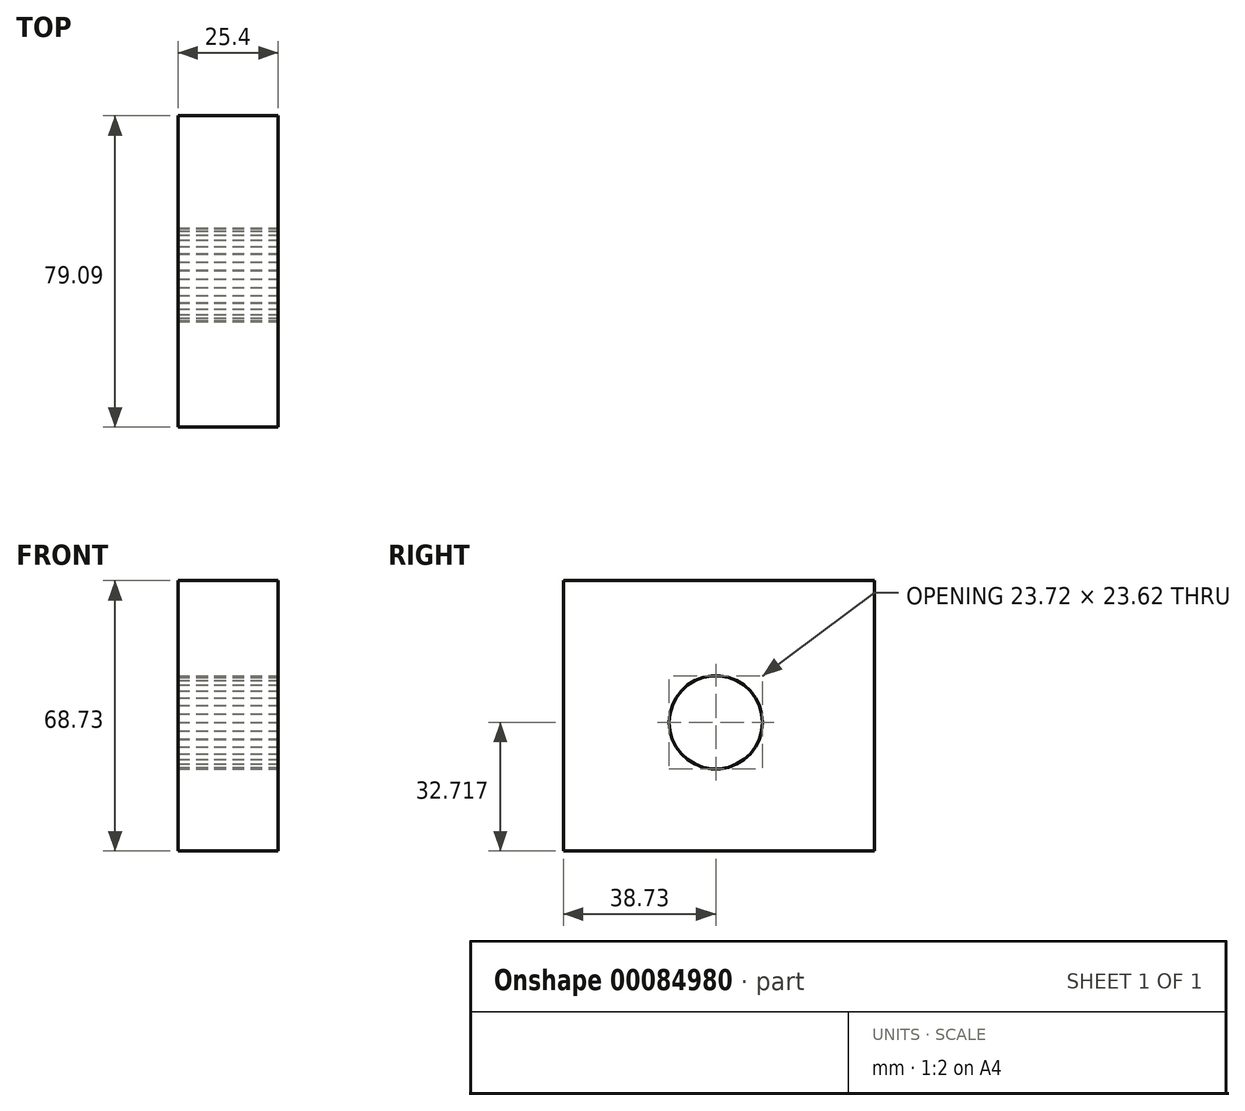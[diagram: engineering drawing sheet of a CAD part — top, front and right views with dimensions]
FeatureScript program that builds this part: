
annotation { "Feature Type Name" : "Feature", "Feature Type Description" : "" }
export const myFeature = defineFeature(function(context is Context, id is Id, definition is map)
    precondition{}
    {
        {
            var Q0;
            Q0=qCreatedBy(makeId("Right.planeOp"),FACE);
            var sketch = newSketch(context, id + "F0", { "sketchPlane" : qUnion([Q0])});
            skLineSegment(sketch, "E0.bottom", {"start": v(-38.73, 43.14) * mm, "end": v(40.36, 43.14) * mm});
            skLineSegment(sketch, "E0.top", {"start": v(-38.73, -25.6) * mm, "end": v(40.36, -25.6) * mm});
            skLineSegment(sketch, "E0.left", {"start": v(-38.73, 43.14) * mm, "end": v(-38.73, -25.6) * mm});
            skLineSegment(sketch, "E0.right", {"start": v(40.36, 43.14) * mm, "end": v(40.36, -25.6) * mm});
            skSolve(sketch);
        }
        {
            var Q0;
            Q0 = qSketchRegion(id + "F0", true);
            extrude(context, id + "F1", {"entities" : qUnion([Q0]), "depth" : 25.4 * mm, "offsetDistance" : 25.4 * mm});
        }
        {
            var Q0;
            Q0=makeQuery(id+"F1.opExtrude","CAP_FACE",FACE,{"disambiguationData":[OSD([sQuery(id+"F0.wireOp",EDGE,"E0.bottom"),sQuery(id+"F0.wireOp",EDGE,"E0.top"),sQuery(id+"F0.wireOp",EDGE,"E0.left"),sQuery(id+"F0.wireOp",EDGE,"E0.right")])],"isStart":false});
            var sketch = newSketch(context, id + "F2", { "sketchPlane" : qUnion([Q0])});
            skCircle(sketch, "E1.cCircle", {"center": v(0, 7.13) * mm, "radius": 11.8 * mm, "construction": true});
            skLineSegment(sketch, "E1.0", {"start": v(10.07, 0.87) * mm, "end": v(8.75, -0.87) * mm});
            skLineSegment(sketch, "E1.1", {"start": v(8.75, -0.87) * mm, "end": v(7.13, -2.34) * mm});
            skLineSegment(sketch, "E1.2", {"start": v(7.13, -2.34) * mm, "end": v(5.27, -3.5) * mm});
            skLineSegment(sketch, "E1.3", {"start": v(5.27, -3.5) * mm, "end": v(3.23, -4.28) * mm});
            skLineSegment(sketch, "E1.4", {"start": v(3.23, -4.28) * mm, "end": v(1.08, -4.68) * mm});
            skLineSegment(sketch, "E1.5", {"start": v(1.08, -4.68) * mm, "end": v(-1.1, -4.68) * mm});
            skLineSegment(sketch, "E1.6", {"start": v(-1.1, -4.68) * mm, "end": v(-3.26, -4.27) * mm});
            skLineSegment(sketch, "E1.7", {"start": v(-3.26, -4.27) * mm, "end": v(-5.3, -3.48) * mm});
            skLineSegment(sketch, "E1.8", {"start": v(-5.3, -3.48) * mm, "end": v(-7.16, -2.33) * mm});
            skLineSegment(sketch, "E1.9", {"start": v(-7.16, -2.33) * mm, "end": v(-8.77, -0.85) * mm});
            skLineSegment(sketch, "E1.10", {"start": v(-8.77, -0.85) * mm, "end": v(-10.09, 0.9) * mm});
            skLineSegment(sketch, "E1.11", {"start": v(-10.09, 0.9) * mm, "end": v(-11.06, 2.86) * mm});
            skLineSegment(sketch, "E1.12", {"start": v(-11.06, 2.86) * mm, "end": v(-11.66, 4.96) * mm});
            skLineSegment(sketch, "E1.13", {"start": v(-11.66, 4.96) * mm, "end": v(-11.86, 7.14) * mm});
            skLineSegment(sketch, "E1.14", {"start": v(-11.86, 7.14) * mm, "end": v(-11.65, 9.32) * mm});
            skLineSegment(sketch, "E1.15", {"start": v(-11.65, 9.32) * mm, "end": v(-11.05, 11.42) * mm});
            skLineSegment(sketch, "E1.16", {"start": v(-11.05, 11.42) * mm, "end": v(-10.07, 13.38) * mm});
            skLineSegment(sketch, "E1.17", {"start": v(-10.07, 13.38) * mm, "end": v(-8.75, 15.13) * mm});
            skLineSegment(sketch, "E1.18", {"start": v(-8.75, 15.13) * mm, "end": v(-7.13, 16.6) * mm});
            skLineSegment(sketch, "E1.19", {"start": v(-7.13, 16.6) * mm, "end": v(-5.27, 17.75) * mm});
            skLineSegment(sketch, "E1.20", {"start": v(-5.27, 17.75) * mm, "end": v(-3.23, 18.54) * mm});
            skLineSegment(sketch, "E1.21", {"start": v(-3.23, 18.54) * mm, "end": v(-1.08, 18.94) * mm});
            skLineSegment(sketch, "E1.22", {"start": v(-1.08, 18.94) * mm, "end": v(1.1, 18.93) * mm});
            skLineSegment(sketch, "E1.23", {"start": v(1.1, 18.93) * mm, "end": v(3.26, 18.53) * mm});
            skLineSegment(sketch, "E1.24", {"start": v(3.26, 18.53) * mm, "end": v(5.3, 17.74) * mm});
            skLineSegment(sketch, "E1.25", {"start": v(5.3, 17.74) * mm, "end": v(7.16, 16.58) * mm});
            skLineSegment(sketch, "E1.26", {"start": v(7.16, 16.58) * mm, "end": v(8.77, 15.1) * mm});
            skLineSegment(sketch, "E1.27", {"start": v(8.77, 15.1) * mm, "end": v(10.09, 13.36) * mm});
            skLineSegment(sketch, "E1.28", {"start": v(10.09, 13.36) * mm, "end": v(11.06, 11.4) * mm});
            skLineSegment(sketch, "E1.29", {"start": v(11.06, 11.4) * mm, "end": v(11.66, 9.3) * mm});
            skLineSegment(sketch, "E1.30", {"start": v(11.66, 9.3) * mm, "end": v(11.86, 7.11) * mm});
            skLineSegment(sketch, "E1.31", {"start": v(11.86, 7.11) * mm, "end": v(11.65, 4.93) * mm});
            skLineSegment(sketch, "E1.32", {"start": v(11.65, 4.93) * mm, "end": v(11.05, 2.83) * mm});
            skLineSegment(sketch, "E1.33", {"start": v(11.05, 2.83) * mm, "end": v(10.07, 0.87) * mm});
            skPoint(sketch, "E1.0.midPoint", {"position": v(9.41, 0) * mm});
            skSolve(sketch);
        }
        {
            var Q0;
            Q0 = qSketchRegion(id + "F2", true);
            extrude(context, id + "F3", {"entities" : qUnion([Q0]), "operationType" : NewBodyOperationType.REMOVE, "oppositeDirection" : true, "depth" : 25.4 * mm, "offsetDistance" : 25.4 * mm});
        }
    });
